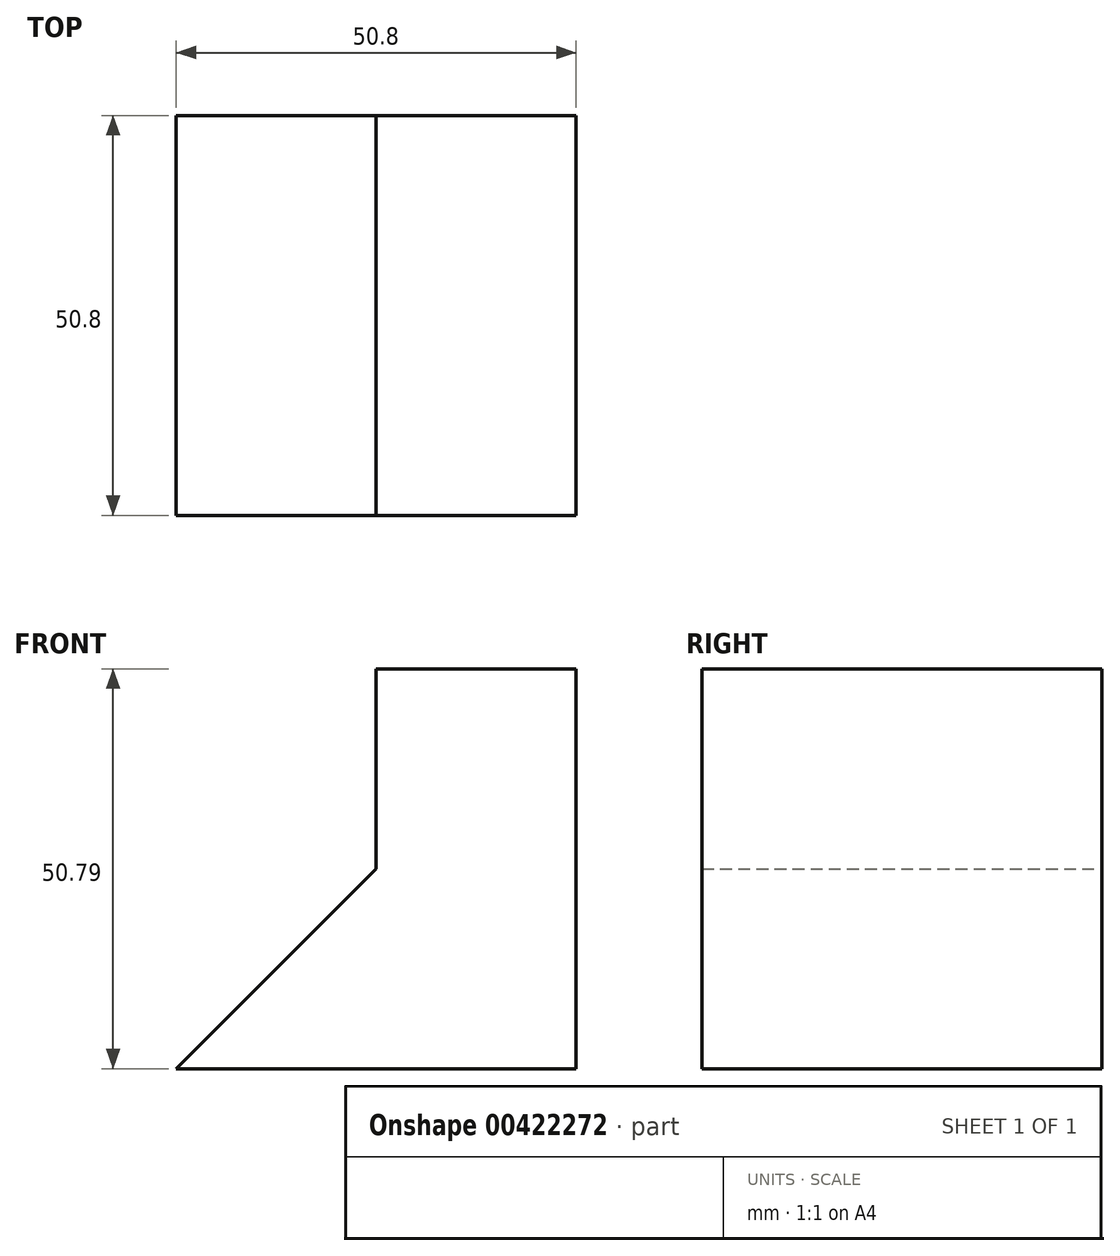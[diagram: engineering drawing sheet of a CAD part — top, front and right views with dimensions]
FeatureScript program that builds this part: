
annotation { "Feature Type Name" : "Feature", "Feature Type Description" : "" }
export const myFeature = defineFeature(function(context is Context, id is Id, definition is map)
    precondition{}
    {
        {
            var Q0;
            Q0=qCreatedBy(makeId("Front.planeOp"),FACE);
            var sketch = newSketch(context, id + "F0", { "sketchPlane" : qUnion([Q0])});
            skLineSegment(sketch, "E0", {"start": v(-27.5, -31.89) * mm, "end": v(23.3, -31.89) * mm});
            skLineSegment(sketch, "E1", {"start": v(23.3, -31.89) * mm, "end": v(23.3, 18.9) * mm});
            skLineSegment(sketch, "E2", {"start": v(23.3, 18.9) * mm, "end": v(-2.1, 18.9) * mm});
            skLineSegment(sketch, "E3", {"start": v(-2.1, 18.9) * mm, "end": v(-2.1, -6.5) * mm});
            skLineSegment(sketch, "E4", {"start": v(-2.1, -6.5) * mm, "end": v(-27.5, -31.89) * mm});
            skSolve(sketch);
        }
        {
            var Q0;
            Q0=makeQuery(id+"F0.imprint","IMPRINT",FACE,{"disambiguationData":[TD([[makeQuery(id+"F0.imprint","IMPRINT",EDGE,{"derivedFrom":sQuery(id+"F0.wireOp",EDGE,"E0")}),1.0]])]});
            extrude(context, id + "F1", {"entities" : qUnion([Q0]), "depth" : 50.8 * mm});
        }
    });
